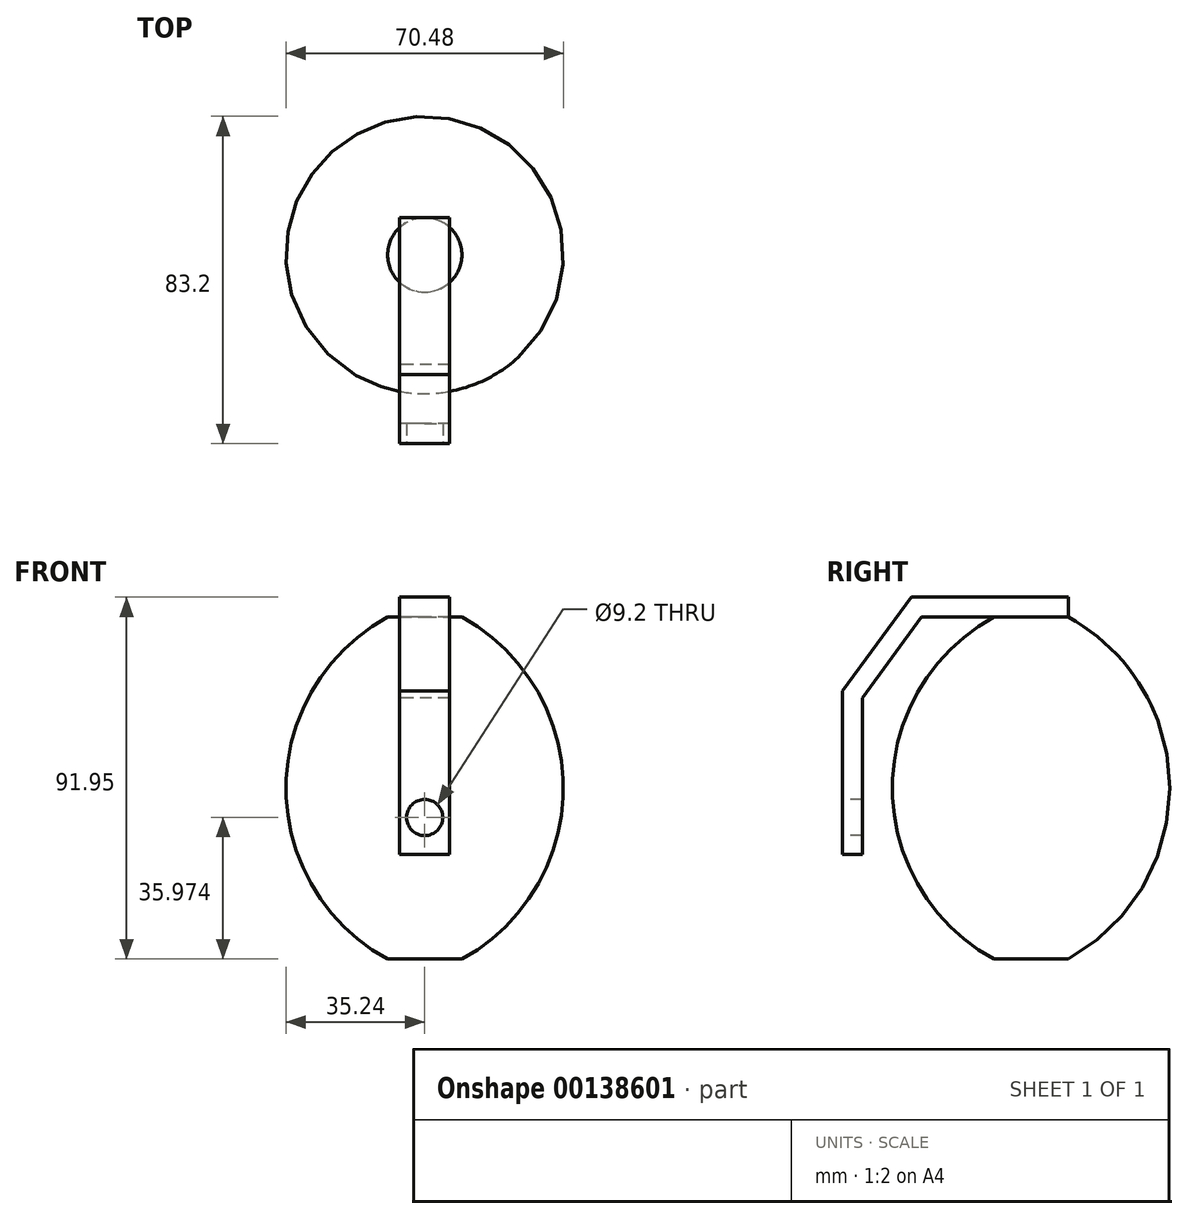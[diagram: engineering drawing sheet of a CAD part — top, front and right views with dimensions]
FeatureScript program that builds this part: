
annotation { "Feature Type Name" : "Feature", "Feature Type Description" : "" }
export const myFeature = defineFeature(function(context is Context, id is Id, definition is map)
    precondition{}
    {
        {
            var Q0;
            Q0=qCreatedBy(makeId("Right.planeOp"),FACE);
            var sketch = newSketch(context, id + "F0", { "sketchPlane" : qUnion([Q0])});
            skArc(sketch, "E0", {"start": v(-9.43, 86.87) * mm, "mid": v(-35.24, 43.44) * mm, "end": v(-9.43, 0) * mm});
            skLineSegment(sketch, "E1", {"start": v(-9.43, 0) * mm, "end": v(0, 0) * mm});
            skLineSegment(sketch, "E2", {"start": v(-9.43, 86.87) * mm, "end": v(0, 86.87) * mm});
            skLineSegment(sketch, "E3", {"start": v(0, 0) * mm, "end": v(0, 86.87) * mm});
            skSolve(sketch);
        }
        {
            var Q0;
            Q0 = qSketchRegion(id + "F0", true);
            var Q1;
            Q1=sQuery(id+"F0.wireOp",EDGE,"E3");
            revolve(context, id + "F1", {"entities" : qUnion([Q0]), "axis" : qUnion([Q1]), "revolveType" : RevolveType.FULL});
        }
        {
            var Q0;
            Q0=qCreatedBy(makeId("Right.planeOp"),FACE);
            var sketch = newSketch(context, id + "F2", { "sketchPlane" : qUnion([Q0])});
            skLineSegment(sketch, "E4.0", {"start": v(9.43, 86.87) * mm, "end": v(-9.43, 86.87) * mm});
            skLineSegment(sketch, "E5", {"start": v(-9.43, 86.87) * mm, "end": v(-27.8, 86.87) * mm});
            skLineSegment(sketch, "E6", {"start": v(-27.8, 86.87) * mm, "end": v(-42.88, 66.4) * mm});
            skLineSegment(sketch, "E7", {"start": v(-42.88, 66.4) * mm, "end": v(-42.88, 26.64) * mm});
            skLineSegment(sketch, "E8.0", {"start": v(-47.96, 68.07) * mm, "end": v(-47.96, 26.64) * mm});
            skLineSegment(sketch, "E8.1", {"start": v(-30.36, 91.95) * mm, "end": v(-47.96, 68.07) * mm});
            skLineSegment(sketch, "E8.2", {"start": v(-9.43, 91.95) * mm, "end": v(-30.36, 91.95) * mm});
            skLineSegment(sketch, "E8.3", {"start": v(9.43, 91.95) * mm, "end": v(-9.43, 91.95) * mm});
            skLineSegment(sketch, "E9", {"start": v(9.43, 86.87) * mm, "end": v(9.43, 91.95) * mm});
            skLineSegment(sketch, "E10", {"start": v(-42.88, 26.64) * mm, "end": v(-47.96, 26.64) * mm});
            skSolve(sketch);
        }
        {
            var Q0;
            Q0 = qSketchRegion(id + "F2", true);
            extrude(context, id + "F3", {"entities" : qUnion([Q0]), "operationType" : NewBodyOperationType.ADD, "endBound" : BoundingType.SYMMETRIC, "depth" : 12.7 * mm});
        }
        {
            var Q0;
            Q0=makeQuery(id+"F3.opExtrude","SWEPT_FACE",FACE,{"disambiguationData":[OSD([sQuery(id+"F2.wireOp",EDGE,"E8.0")])]});
            var sketch = newSketch(context, id + "F4", { "sketchPlane" : qUnion([Q0])});
            skCircle(sketch, "E11", {"center": v(0, 35.97) * mm, "radius": 4.6 * mm});
            skSolve(sketch);
        }
        {
            var Q0;
            Q0 = qSketchRegion(id + "F4", true);
            extrude(context, id + "F5", {"entities" : qUnion([Q0]), "operationType" : NewBodyOperationType.REMOVE, "endBound" : BoundingType.UP_TO_NEXT, "oppositeDirection" : true, "depth" : 25.4 * mm});
        }
    });
